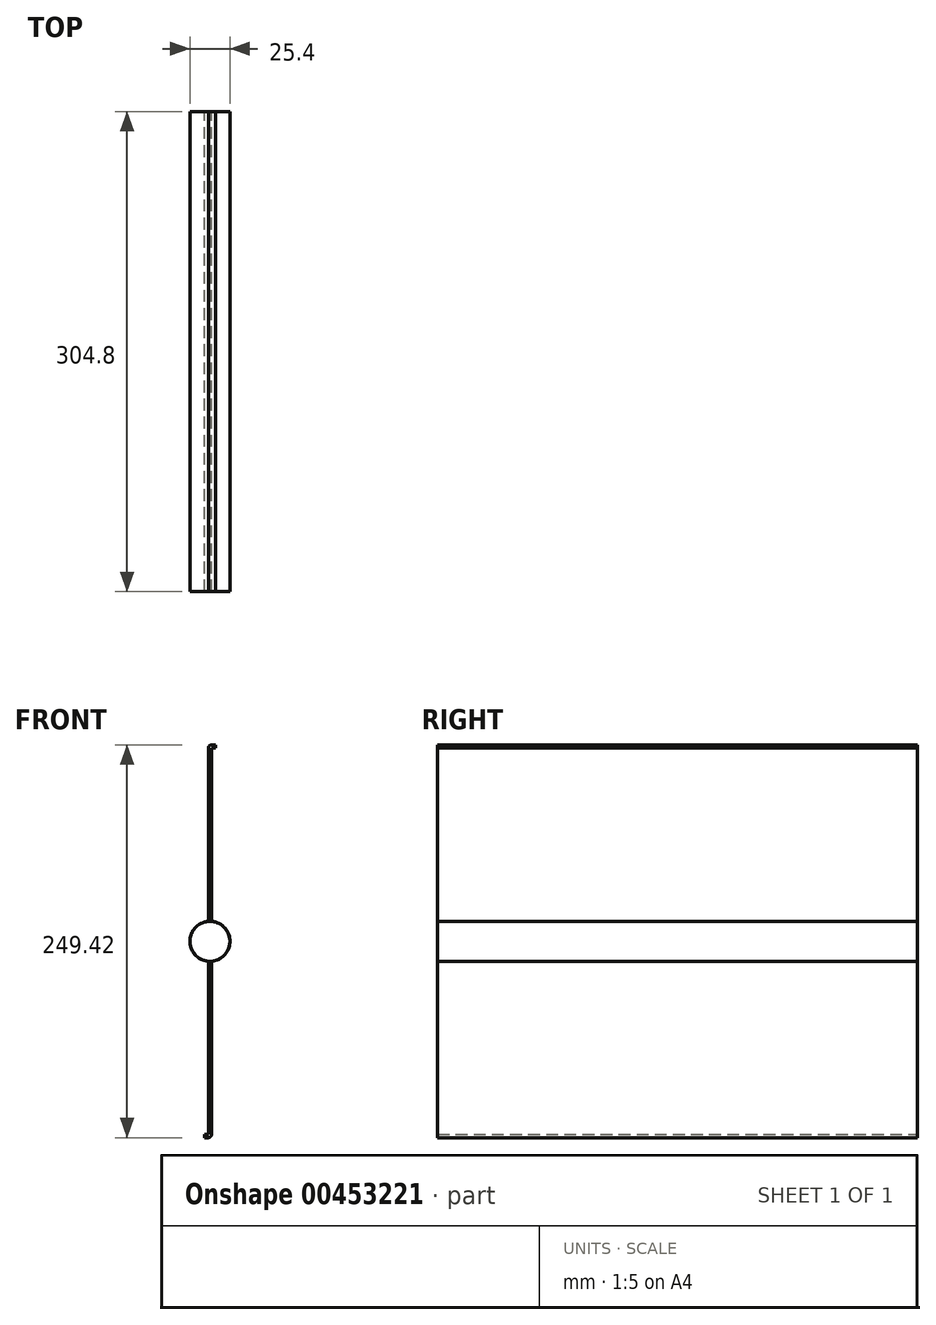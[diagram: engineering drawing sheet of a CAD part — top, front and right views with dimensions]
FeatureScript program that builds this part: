
annotation { "Feature Type Name" : "Feature", "Feature Type Description" : "" }
export const myFeature = defineFeature(function(context is Context, id is Id, definition is map)
    precondition{}
    {
        {
            var Q0;
            Q0=qCreatedBy(makeId("Front.planeOp"),FACE);
            var sketch = newSketch(context, id + "F0", { "sketchPlane" : qUnion([Q0])});
            skCircle(sketch, "E0", {"center": v(0, 0) * mm, "radius": 12.7 * mm});
            skLineSegment(sketch, "E1", {"start": v(-1, 12.66) * mm, "end": v(-1, 122.71) * mm});
            skLineSegment(sketch, "E2", {"start": v(1, 12.66) * mm, "end": v(1, 122.71) * mm});
            skArc(sketch, "E3", {"start": v(-1, 122.71) * mm, "mid": v(-0.41, 124.11) * mm, "end": v(1, 124.7) * mm});
            skLineSegment(sketch, "E4", {"start": v(1, 124.7) * mm, "end": v(3.53, 124.71) * mm});
            skLineSegment(sketch, "E5", {"start": v(3.53, 124.71) * mm, "end": v(3.53, 122.71) * mm});
            skLineSegment(sketch, "E6", {"start": v(3.53, 122.71) * mm, "end": v(1, 122.71) * mm});
            skLineSegment(sketch, "E7", {"start": v(-1, 12.66) * mm, "end": v(1, 12.66) * mm});
            skLineSegment(sketch, "E8", {"start": v(1, 122.71) * mm, "end": v(3.53, 122.71) * mm});
            skLineSegment(sketch, "E9", {"start": v(3.53, 122.71) * mm, "end": v(3.53, 124.71) * mm});
            skLineSegment(sketch, "E10", {"start": v(3.53, 124.71) * mm, "end": v(1, 124.7) * mm});
            skArc(sketch, "E11", {"start": v(1, 124.7) * mm, "mid": v(-0.41, 124.11) * mm, "end": v(-1, 122.71) * mm});
            skLineSegment(sketch, "E12", {"start": v(-1, 122.71) * mm, "end": v(-1, 12.66) * mm});
            skSolve(sketch);
        }
        {
            var Q0;
            Q0 = qSketchRegion(id + "F0", true);
            extrude(context, id + "F1", {"entities" : qUnion([Q0]), "endBound" : BoundingType.SYMMETRIC, "depth" : 304.8 * mm});
        }
        {
            var Q0;
            Q0=qCreatedBy(makeId("Right.planeOp"),FACE);
            var sketch = newSketch(context, id + "F2", { "sketchPlane" : qUnion([Q0])});
            skLineSegment(sketch, "E13", {"start": v(0, 0) * mm, "end": v(68.33, 0) * mm});
            skSolve(sketch);
        }
        {
            var Q0;
            Q0=makeQuery(id+"F1.opExtrude","SWEPT_BODY",BODY,{"disambiguationData":[OSD([sQuery(id+"F0.wireOp",EDGE,"E0"),sQuery(id+"F0.wireOp",EDGE,"E2"),sQuery(id+"F0.wireOp",EDGE,"E8"),sQuery(id+"F0.wireOp",EDGE,"E9"),sQuery(id+"F0.wireOp",EDGE,"E10"),sQuery(id+"F0.wireOp",EDGE,"E11"),sQuery(id+"F0.wireOp",EDGE,"E12")])]});
            var Q1;
            Q1=sQuery(id+"F2.wireOp",EDGE,"E13");
            circularPattern(context, id + "F3", {"entities" : qUnion([Q0]), "axis" : qUnion([Q1]), "angle" : 360 * degree, "instanceCount" : 2, "equalSpace" : true});
        }
    });
